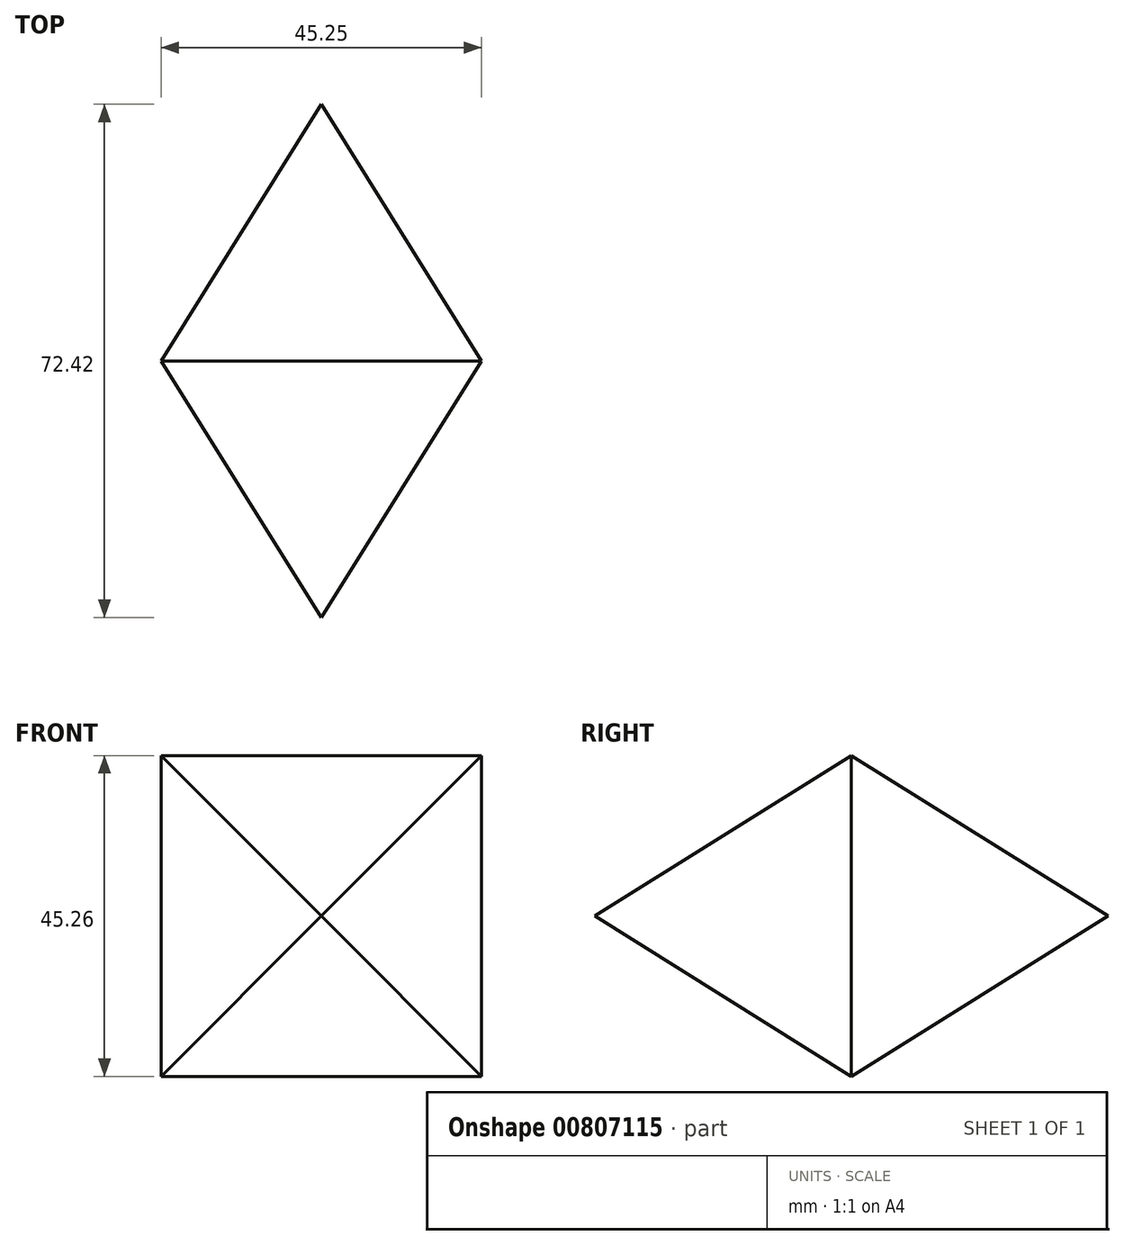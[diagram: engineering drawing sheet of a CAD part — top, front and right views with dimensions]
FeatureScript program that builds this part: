
annotation { "Feature Type Name" : "Feature", "Feature Type Description" : "" }
export const myFeature = defineFeature(function(context is Context, id is Id, definition is map)
    precondition{}
    {
        {
            var Q0;
            Q0=qCreatedBy(makeId("Front.planeOp"),FACE);
            var sketch = newSketch(context, id + "F0", { "sketchPlane" : qUnion([Q0])});
            skLineSegment(sketch, "E0.bottom", {"start": v(-32.5, -14.5) * mm, "end": v(12.75, -14.5) * mm});
            skLineSegment(sketch, "E0.top", {"start": v(-32.5, 30.75) * mm, "end": v(12.75, 30.75) * mm});
            skLineSegment(sketch, "E0.left", {"start": v(-32.5, -14.5) * mm, "end": v(-32.5, 30.75) * mm});
            skLineSegment(sketch, "E0.right", {"start": v(12.75, -14.5) * mm, "end": v(12.75, 30.75) * mm});
            skPoint(sketch, "E0.middle", {"position": v(-9.88, 8.12) * mm});
            skSolve(sketch);
        }
        {
            var Q0;
            Q0=makeQuery(id+"F0.imprint","IMPRINT",FACE,{"disambiguationData":[TD([[makeQuery(id+"F0.imprint","IMPRINT",EDGE,{"derivedFrom":sQuery(id+"F0.wireOp",EDGE,"E0.bottom")}),1.0]])]});
            extrude(context, id + "F1", {"entities" : qUnion([Q0]), "oppositeDirection" : true, "depth" : 72.9 * mm, "offsetDistance" : 25.4 * mm, "hasDraft" : true, "draftAngle" : 32 * degree, "draftPullDirection" : true, "hasSecondDirection" : true, "secondDirectionOppositeDirection" : false, "secondDirectionDepth" : 72.9 * mm, "hasSecondDirectionDraft" : true, "secondDirectionDraftAngle" : 32 * degree, "secondDirectionDraftPullDirection" : true});
        }
    });
